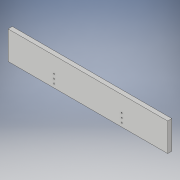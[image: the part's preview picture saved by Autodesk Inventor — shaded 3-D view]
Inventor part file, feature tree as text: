
AUTODESK INVENTOR PART (.ipt)
format: ipt  version: 2018 (Build 220112000, 112)  size: 111,104 bytes
history: native  units: in
note: dims shown in document units (in); Inventor stores cm internally (conversion verified against a paired STEP export)
features: extrude x2, sketch x2
ambient origin geometry x8: Origin, YZ Plane, XZ Plane, XY Plane, X Axis, Y Axis, Z Axis, Center Point
bodies: Solid1 (feature_tree)
feature tree (4):
  extrude  "Extrusion1"  Depth=5.0in
  extrude  "Extrusion2"  Depth=0.75in
  sketch  "Sketch1"  dims[d0=28.31in d1=5.0in]
  sketch  "Sketch2"  dims[d2=0.75in d3=0.0in d4=8.155in d5=0.67in d6=0.75in d7=0.75in d8=0.21in d9=0.75in d10=0.0in]
